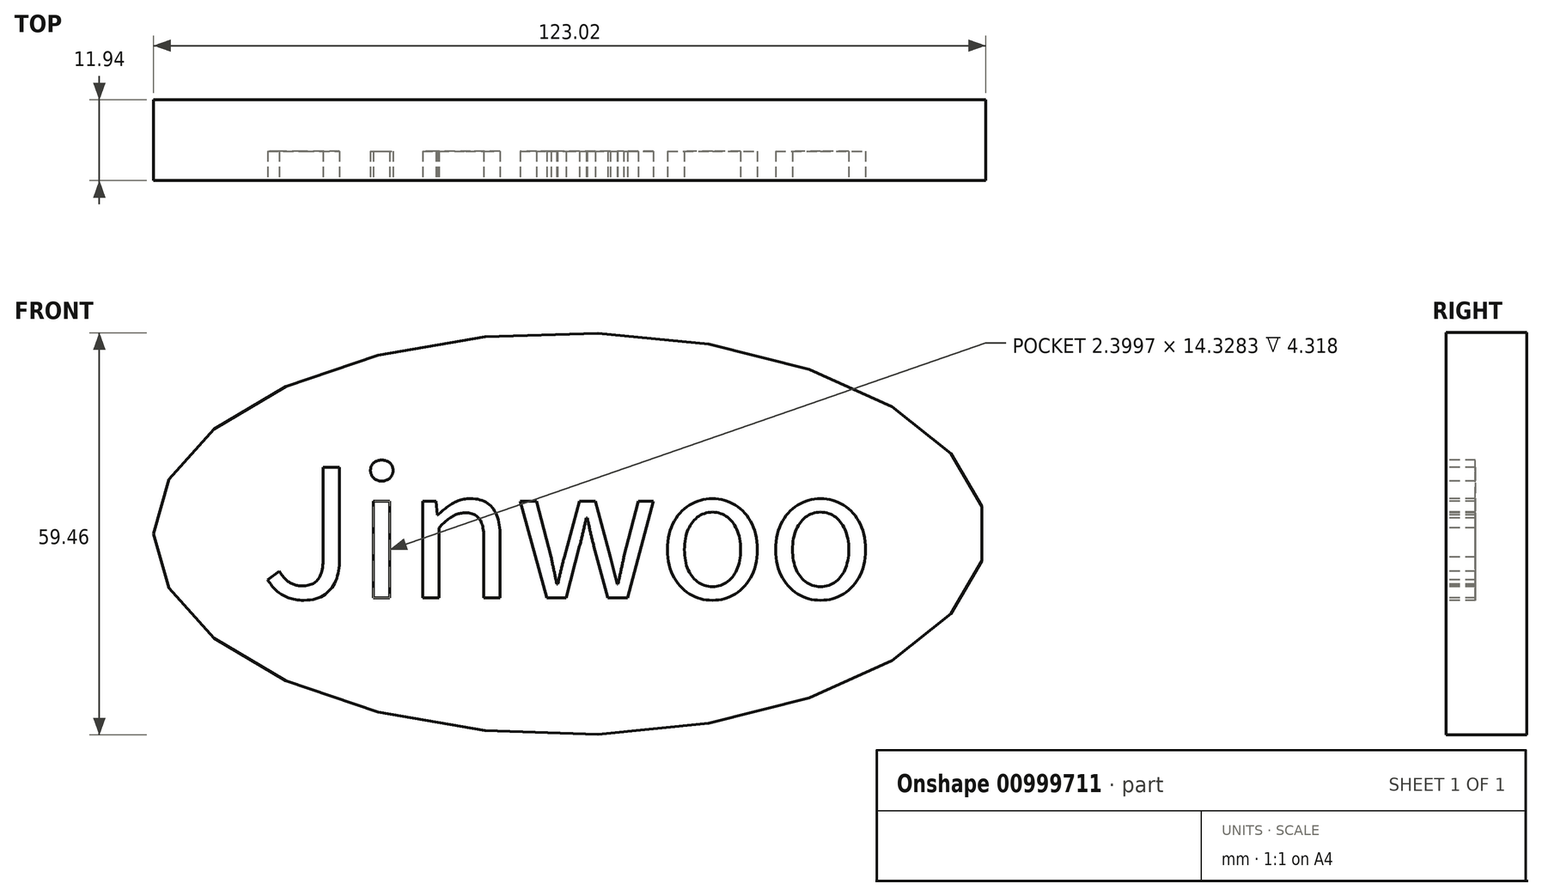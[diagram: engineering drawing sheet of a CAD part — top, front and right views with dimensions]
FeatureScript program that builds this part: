
annotation { "Feature Type Name" : "Feature", "Feature Type Description" : "" }
export const myFeature = defineFeature(function(context is Context, id is Id, definition is map)
    precondition{}
    {
        {
            var Q0;
            Q0=qCreatedBy(makeId("Front.planeOp"),FACE);
            var sketch = newSketch(context, id + "F0", { "sketchPlane" : qUnion([Q0])});
            skEllipse(sketch, "E0", {"center": v(0, 0) * mm, "majorRadius": 61.51 * mm, "minorRadius": 29.73 * mm, "majorAxis": v(-1, 0)});
            skSolve(sketch);
        }
        {
            var Q0;
            Q0=makeQuery(id+"F0.imprint","IMPRINT",FACE,{"disambiguationData":[TD([[makeQuery(id+"F0.imprint","IMPRINT",EDGE,{"derivedFrom":sQuery(id+"F0.wireOp",EDGE,"E0")}),1.0]])]});
            extrude(context, id + "F1", {"entities" : qUnion([Q0]), "depth" : 11.94 * mm, "offsetDistance" : 25.4 * mm});
        }
        {
            var Q0;
            Q0=makeQuery(id+"F1.opExtrude","CAP_FACE",FACE,{"disambiguationData":[OSD([sQuery(id+"F0.wireOp",EDGE,"E0")])],"isStart":false});
            var sketch = newSketch(context, id + "F2", { "sketchPlane" : qUnion([Q0])});
            skText(sketch, "E1", { "text": "Jinwoo", "fontName": "NotoSansCJKkr-Regular.otf"});
            const initialGuessF2  = {"E1": [-0.04555, -0.0095, 1, 0, 0.019]};
            skSetInitialGuess(sketch, initialGuessF2);
            skSolve(sketch);
        }
        {
            var Q0;
            Q0 = qSketchRegion(id + "F2", true);
            extrude(context, id + "F3", {"entities" : qUnion([Q0]), "operationType" : NewBodyOperationType.REMOVE, "oppositeDirection" : true, "depth" : 4.32 * mm, "offsetDistance" : 25.4 * mm});
        }
    });
